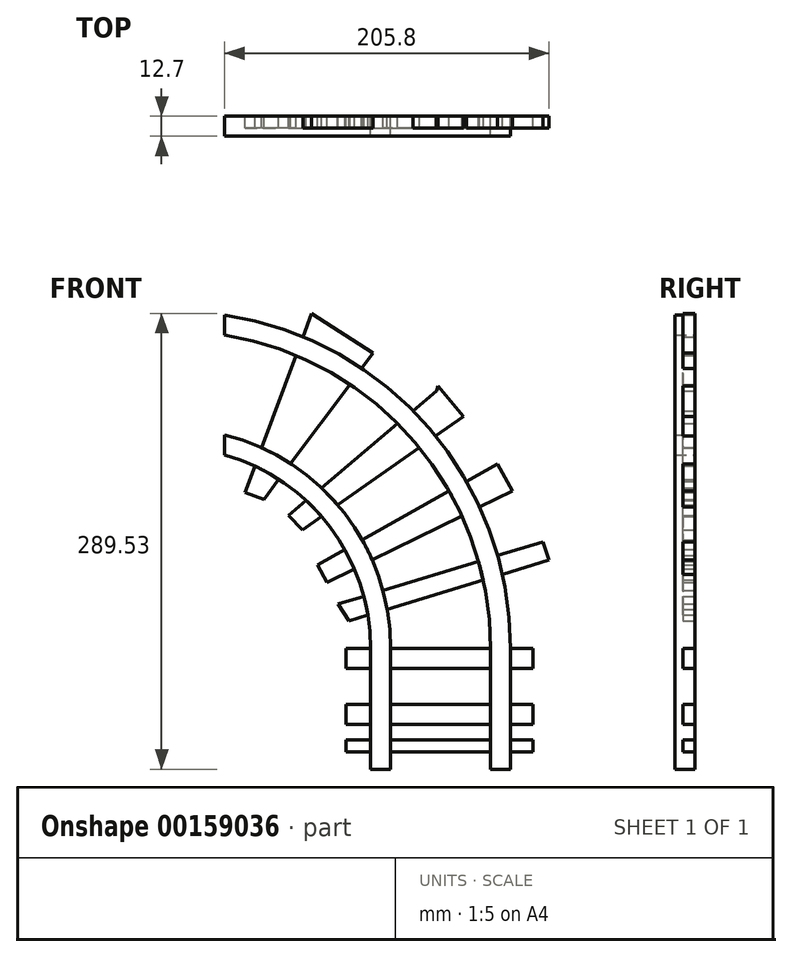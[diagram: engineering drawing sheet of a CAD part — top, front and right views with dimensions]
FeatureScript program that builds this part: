
annotation { "Feature Type Name" : "Feature", "Feature Type Description" : "" }
export const myFeature = defineFeature(function(context is Context, id is Id, definition is map)
    precondition{}
    {
        {
            var Q0;
            Q0=qCreatedBy(makeId("Front.planeOp"),FACE);
            var sketch = newSketch(context, id + "F0", { "sketchPlane" : qUnion([Q0])});
            skLineSegment(sketch, "E0", {"start": v(-50.34, 0) * mm, "end": v(-37.64, 0) * mm});
            skLineSegment(sketch, "E1", {"start": v(-37.64, 0) * mm, "end": v(-37.64, -76.88) * mm});
            skLineSegment(sketch, "E2", {"start": v(-50.34, 0) * mm, "end": v(-50.34, -76.88) * mm});
            skLineSegment(sketch, "E3", {"start": v(-50.34, -76.88) * mm, "end": v(-37.64, -76.88) * mm});
            skLineSegment(sketch, "E4", {"start": v(25.86, 0) * mm, "end": v(25.86, -76.88) * mm});
            skLineSegment(sketch, "E5", {"start": v(25.86, -76.88) * mm, "end": v(38.56, -76.88) * mm});
            skLineSegment(sketch, "E6", {"start": v(38.56, -76.88) * mm, "end": v(38.56, 0) * mm});
            skLineSegment(sketch, "E7", {"start": v(38.56, 0) * mm, "end": v(25.86, 0) * mm});
            skArc(sketch, "E8", {"start": v(-50.34, 0) * mm, "mid": v(-76.12, 76.94) * mm, "end": v(-143.03, 122.84) * mm});
            skArc(sketch, "E9", {"start": v(-37.64, 0) * mm, "mid": v(-67.1, 85.84) * mm, "end": v(-143.03, 135.54) * mm});
            skArc(sketch, "E10", {"start": v(25.86, 0) * mm, "mid": v(-22.06, 130.52) * mm, "end": v(-143.03, 199.04) * mm});
            skArc(sketch, "E11", {"start": v(38.56, 0) * mm, "mid": v(-13.06, 139.47) * mm, "end": v(-143.03, 211.74) * mm});
            skLineSegment(sketch, "E12", {"start": v(-143.03, 211.74) * mm, "end": v(-143.03, 199.04) * mm});
            skLineSegment(sketch, "E13", {"start": v(-143.03, 135.54) * mm, "end": v(-143.03, 122.84) * mm});
            skLineSegment(sketch, "E14", {"start": v(-65.9, -35.56) * mm, "end": v(-65.9, -48.26) * mm});
            skLineSegment(sketch, "E15", {"start": v(-65.9, -48.26) * mm, "end": v(52.66, -48.26) * mm});
            skLineSegment(sketch, "E16", {"start": v(52.66, -48.26) * mm, "end": v(52.66, -35.56) * mm});
            skLineSegment(sketch, "E17", {"start": v(52.66, -35.56) * mm, "end": v(-65.9, -35.56) * mm});
            skLineSegment(sketch, "E18", {"start": v(-65.9, 0) * mm, "end": v(-65.9, -12.7) * mm});
            skLineSegment(sketch, "E19", {"start": v(-65.9, -12.7) * mm, "end": v(52.66, -12.7) * mm});
            skLineSegment(sketch, "E20", {"start": v(52.66, -12.7) * mm, "end": v(52.66, 0) * mm});
            skLineSegment(sketch, "E21", {"start": v(52.66, 0) * mm, "end": v(-65.9, 0) * mm});
            skLineSegment(sketch, "E22", {"start": v(-48.75, 187.4) * mm, "end": v(-87.85, 212.65) * mm});
            skLineSegment(sketch, "E23", {"start": v(-87.85, 212.65) * mm, "end": v(-130.11, 98.99) * mm});
            skLineSegment(sketch, "E24", {"start": v(-130.11, 98.99) * mm, "end": v(-118.21, 94.56) * mm});
            skLineSegment(sketch, "E25", {"start": v(-118.21, 94.56) * mm, "end": v(-48.75, 187.4) * mm});
            skLineSegment(sketch, "E26", {"start": v(-78.05, 41.82) * mm, "end": v(-84.25, 52.9) * mm});
            skLineSegment(sketch, "E27", {"start": v(-84.25, 52.9) * mm, "end": v(30.17, 116.9) * mm});
            skLineSegment(sketch, "E28", {"start": v(39.65, 99.94) * mm, "end": v(-78.05, 41.82) * mm});
            skLineSegment(sketch, "E29", {"start": v(30.17, 116.9) * mm, "end": v(39.65, 99.94) * mm});
            skLineSegment(sketch, "E30", {"start": v(39.65, 99.94) * mm, "end": v(39.65, 99.94) * mm});
            skLineSegment(sketch, "E31", {"start": v(-70.95, 28) * mm, "end": v(59.22, 67.6) * mm});
            skLineSegment(sketch, "E32", {"start": v(59.22, 67.6) * mm, "end": v(62.77, 55.95) * mm});
            skLineSegment(sketch, "E33", {"start": v(62.77, 55.95) * mm, "end": v(-63.98, 17.37) * mm});
            skLineSegment(sketch, "E34", {"start": v(-70.95, 28) * mm, "end": v(-63.98, 17.37) * mm});
            skLineSegment(sketch, "E35", {"start": v(-102.62, 84.2) * mm, "end": v(-93.77, 75.1) * mm});
            skLineSegment(sketch, "E36", {"start": v(-102.62, 84.2) * mm, "end": v(-8.48, 163.47) * mm});
            skLineSegment(sketch, "E37", {"start": v(-93.77, 75.1) * mm, "end": v(8.75, 147.3) * mm});
            skLineSegment(sketch, "E38", {"start": v(8.75, 147.3) * mm, "end": v(-7.49, 166.59) * mm});
            skLineSegment(sketch, "E39", {"start": v(-7.49, 166.59) * mm, "end": v(-8.48, 163.47) * mm});
            skLineSegment(sketch, "E40", {"start": v(-65.9, -58.2) * mm, "end": v(-65.9, -65.83) * mm});
            skLineSegment(sketch, "E41", {"start": v(-65.9, -65.83) * mm, "end": v(52.66, -65.83) * mm});
            skLineSegment(sketch, "E42", {"start": v(52.66, -65.83) * mm, "end": v(52.66, -58.2) * mm});
            skLineSegment(sketch, "E43", {"start": v(52.66, -58.2) * mm, "end": v(-65.9, -58.2) * mm});
            skSolve(sketch);
        }
        {
            var Q0;
            {var subQ0=sQuery(id+"F0.wireOp",EDGE,"E13");Q0=makeQuery(id+"F0.imprint","IMPRINT",FACE,{"disambiguationData":[TD([[makeQuery(id+"F0.imprint","IMPRINT",EDGE,{"derivedFrom":subQ0}),1.0]])]});}
            var Q1;
            {var subQ0=sQuery(id+"F0.wireOp",EDGE,"E25");var subQ1=sQuery(id+"F0.wireOp",EDGE,"E8");var subQ2=makeQuery(id+"F0.imprint","INTERSECT",VERTEX,{"derivedFrom":[subQ1,subQ0]});Q1=makeQuery(id+"F0.imprint","IMPRINT",FACE,{"disambiguationData":[TD([[makeQuery(id+"F0.imprint","IMPRINT",EDGE,{"disambiguationData":[TD([[subQ2,-1.0]])],"derivedFrom":subQ1}),-1.0]])]});}
            var Q2;
            {var subQ0=sQuery(id+"F0.wireOp",EDGE,"E36");var subQ1=sQuery(id+"F0.wireOp",EDGE,"E8");var subQ2=makeQuery(id+"F0.imprint","INTERSECT",VERTEX,{"derivedFrom":[subQ1,subQ0]});Q2=makeQuery(id+"F0.imprint","IMPRINT",FACE,{"disambiguationData":[TD([[makeQuery(id+"F0.imprint","IMPRINT",EDGE,{"disambiguationData":[TD([[subQ2,-1.0]])],"derivedFrom":subQ1}),-1.0]])]});}
            var Q3;
            {var subQ0=sQuery(id+"F0.wireOp",EDGE,"E37");var subQ1=sQuery(id+"F0.wireOp",EDGE,"E8");var subQ2=makeQuery(id+"F0.imprint","INTERSECT",VERTEX,{"derivedFrom":[subQ1,subQ0]});Q3=makeQuery(id+"F0.imprint","IMPRINT",FACE,{"disambiguationData":[TD([[makeQuery(id+"F0.imprint","IMPRINT",EDGE,{"disambiguationData":[TD([[subQ2,-1.0]])],"derivedFrom":subQ1}),-1.0]])]});}
            var Q4;
            {var subQ0=sQuery(id+"F0.wireOp",EDGE,"E27");var subQ1=sQuery(id+"F0.wireOp",EDGE,"E8");var subQ2=makeQuery(id+"F0.imprint","INTERSECT",VERTEX,{"derivedFrom":[subQ1,subQ0]});Q4=makeQuery(id+"F0.imprint","IMPRINT",FACE,{"disambiguationData":[TD([[makeQuery(id+"F0.imprint","IMPRINT",EDGE,{"disambiguationData":[TD([[subQ2,-1.0]])],"derivedFrom":subQ1}),-1.0]])]});}
            var Q5;
            {var subQ0=sQuery(id+"F0.wireOp",EDGE,"E28");var subQ1=sQuery(id+"F0.wireOp",EDGE,"E8");var subQ2=makeQuery(id+"F0.imprint","INTERSECT",VERTEX,{"derivedFrom":[subQ1,subQ0]});Q5=makeQuery(id+"F0.imprint","IMPRINT",FACE,{"disambiguationData":[TD([[makeQuery(id+"F0.imprint","IMPRINT",EDGE,{"disambiguationData":[TD([[subQ2,-1.0]])],"derivedFrom":subQ1}),-1.0]])]});}
            var Q6;
            {var subQ0=sQuery(id+"F0.wireOp",EDGE,"E31");var subQ1=sQuery(id+"F0.wireOp",EDGE,"E8");var subQ2=makeQuery(id+"F0.imprint","INTERSECT",VERTEX,{"derivedFrom":[subQ1,subQ0]});Q6=makeQuery(id+"F0.imprint","IMPRINT",FACE,{"disambiguationData":[TD([[makeQuery(id+"F0.imprint","IMPRINT",EDGE,{"disambiguationData":[TD([[subQ2,-1.0]])],"derivedFrom":subQ1}),-1.0]])]});}
            var Q7;
            {var subQ0=sQuery(id+"F0.wireOp",EDGE,"E33");var subQ1=sQuery(id+"F0.wireOp",EDGE,"E8");var subQ2=makeQuery(id+"F0.imprint","INTERSECT",VERTEX,{"derivedFrom":[subQ1,subQ0]});Q7=makeQuery(id+"F0.imprint","IMPRINT",FACE,{"disambiguationData":[TD([[makeQuery(id+"F0.imprint","IMPRINT",EDGE,{"disambiguationData":[TD([[subQ2,-1.0]])],"derivedFrom":subQ1}),-1.0]])]});}
            var Q8;
            {var subQ1=sQuery(id+"F0.wireOp",EDGE,"E8");var subQ3=sQuery(id+"F0.wireOp",EDGE,"E33");var subQ4=makeQuery(id+"F0.imprint","INTERSECT",VERTEX,{"derivedFrom":[subQ1,subQ3]});Q8=makeQuery(id+"F0.imprint","IMPRINT",FACE,{"disambiguationData":[TD([[makeQuery(id+"F0.imprint","IMPRINT",EDGE,{"disambiguationData":[TD([[subQ4,1.0]])],"derivedFrom":subQ3}),1.0]])]});}
            var Q9;
            {var subQ3=sQuery(id+"F0.wireOp",EDGE,"E19");var subQ5=sQuery(id+"F0.wireOp",EDGE,"E2");var subQ7=makeQuery(id+"F0.imprint","INTERSECT",VERTEX,{"derivedFrom":[subQ5,subQ3]});Q9=makeQuery(id+"F0.imprint","IMPRINT",FACE,{"disambiguationData":[TD([[makeQuery(id+"F0.imprint","IMPRINT",EDGE,{"disambiguationData":[TD([[subQ7,-1.0]])],"derivedFrom":subQ3}),1.0]])]});}
            var Q10;
            {var subQ0=sQuery(id+"F0.wireOp",EDGE,"E19");var subQ1=sQuery(id+"F0.wireOp",EDGE,"E1");var subQ2=makeQuery(id+"F0.imprint","INTERSECT",VERTEX,{"derivedFrom":[subQ1,subQ0]});Q10=makeQuery(id+"F0.imprint","IMPRINT",FACE,{"disambiguationData":[TD([[makeQuery(id+"F0.imprint","IMPRINT",EDGE,{"disambiguationData":[TD([[subQ2,-1.0]])],"derivedFrom":subQ1}),-1.0]])]});}
            var Q11;
            {var subQ0=sQuery(id+"F0.wireOp",EDGE,"E17");var subQ1=sQuery(id+"F0.wireOp",EDGE,"E1");var subQ2=makeQuery(id+"F0.imprint","INTERSECT",VERTEX,{"derivedFrom":[subQ1,subQ0]});Q11=makeQuery(id+"F0.imprint","IMPRINT",FACE,{"disambiguationData":[TD([[makeQuery(id+"F0.imprint","IMPRINT",EDGE,{"disambiguationData":[TD([[subQ2,-1.0]])],"derivedFrom":subQ1}),-1.0]])]});}
            var Q12;
            {var subQ0=sQuery(id+"F0.wireOp",EDGE,"E15");var subQ1=sQuery(id+"F0.wireOp",EDGE,"E1");var subQ2=makeQuery(id+"F0.imprint","INTERSECT",VERTEX,{"derivedFrom":[subQ1,subQ0]});Q12=makeQuery(id+"F0.imprint","IMPRINT",FACE,{"disambiguationData":[TD([[makeQuery(id+"F0.imprint","IMPRINT",EDGE,{"disambiguationData":[TD([[subQ2,-1.0]])],"derivedFrom":subQ1}),-1.0]])]});}
            var Q13;
            {var subQ0=sQuery(id+"F0.wireOp",EDGE,"E41");var subQ1=sQuery(id+"F0.wireOp",EDGE,"E1");var subQ2=makeQuery(id+"F0.imprint","INTERSECT",VERTEX,{"derivedFrom":[subQ1,subQ0]});Q13=makeQuery(id+"F0.imprint","IMPRINT",FACE,{"disambiguationData":[TD([[makeQuery(id+"F0.imprint","IMPRINT",EDGE,{"disambiguationData":[TD([[subQ2,1.0]])],"derivedFrom":subQ1}),-1.0]])]});}
            var Q14;
            {var subQ0=sQuery(id+"F0.wireOp",EDGE,"E3");Q14=makeQuery(id+"F0.imprint","IMPRINT",FACE,{"disambiguationData":[TD([[makeQuery(id+"F0.imprint","IMPRINT",EDGE,{"derivedFrom":subQ0}),1.0]])]});}
            var Q15;
            {var subQ0=sQuery(id+"F0.wireOp",EDGE,"E5");Q15=makeQuery(id+"F0.imprint","IMPRINT",FACE,{"disambiguationData":[TD([[makeQuery(id+"F0.imprint","IMPRINT",EDGE,{"derivedFrom":subQ0}),1.0]])]});}
            var Q16;
            {var subQ0=sQuery(id+"F0.wireOp",EDGE,"E41");var subQ1=sQuery(id+"F0.wireOp",EDGE,"E4");var subQ2=makeQuery(id+"F0.imprint","INTERSECT",VERTEX,{"derivedFrom":[subQ1,subQ0]});Q16=makeQuery(id+"F0.imprint","IMPRINT",FACE,{"disambiguationData":[TD([[makeQuery(id+"F0.imprint","IMPRINT",EDGE,{"disambiguationData":[TD([[subQ2,1.0]])],"derivedFrom":subQ1}),1.0]])]});}
            var Q17;
            {var subQ0=sQuery(id+"F0.wireOp",EDGE,"E15");var subQ1=sQuery(id+"F0.wireOp",EDGE,"E4");var subQ2=makeQuery(id+"F0.imprint","INTERSECT",VERTEX,{"derivedFrom":[subQ1,subQ0]});Q17=makeQuery(id+"F0.imprint","IMPRINT",FACE,{"disambiguationData":[TD([[makeQuery(id+"F0.imprint","IMPRINT",EDGE,{"disambiguationData":[TD([[subQ2,-1.0]])],"derivedFrom":subQ1}),1.0]])]});}
            var Q18;
            {var subQ0=sQuery(id+"F0.wireOp",EDGE,"E17");var subQ1=sQuery(id+"F0.wireOp",EDGE,"E4");var subQ2=makeQuery(id+"F0.imprint","INTERSECT",VERTEX,{"derivedFrom":[subQ1,subQ0]});Q18=makeQuery(id+"F0.imprint","IMPRINT",FACE,{"disambiguationData":[TD([[makeQuery(id+"F0.imprint","IMPRINT",EDGE,{"disambiguationData":[TD([[subQ2,-1.0]])],"derivedFrom":subQ1}),1.0]])]});}
            var Q19;
            {var subQ0=sQuery(id+"F0.wireOp",EDGE,"E19");var subQ1=sQuery(id+"F0.wireOp",EDGE,"E4");var subQ2=makeQuery(id+"F0.imprint","INTERSECT",VERTEX,{"derivedFrom":[subQ1,subQ0]});Q19=makeQuery(id+"F0.imprint","IMPRINT",FACE,{"disambiguationData":[TD([[makeQuery(id+"F0.imprint","IMPRINT",EDGE,{"disambiguationData":[TD([[subQ2,-1.0]])],"derivedFrom":subQ1}),1.0]])]});}
            var Q20;
            {var subQ3=sQuery(id+"F0.wireOp",EDGE,"E19");var subQ5=sQuery(id+"F0.wireOp",EDGE,"E6");var subQ7=makeQuery(id+"F0.imprint","INTERSECT",VERTEX,{"derivedFrom":[subQ5,subQ3]});Q20=makeQuery(id+"F0.imprint","IMPRINT",FACE,{"disambiguationData":[TD([[makeQuery(id+"F0.imprint","IMPRINT",EDGE,{"disambiguationData":[TD([[subQ7,1.0]])],"derivedFrom":subQ3}),1.0]])]});}
            var Q21;
            {var subQ3=sQuery(id+"F0.wireOp",EDGE,"E33");var subQ5=sQuery(id+"F0.wireOp",EDGE,"E11");var subQ6=makeQuery(id+"F0.imprint","INTERSECT",VERTEX,{"derivedFrom":[subQ5,subQ3]});Q21=makeQuery(id+"F0.imprint","IMPRINT",FACE,{"disambiguationData":[TD([[makeQuery(id+"F0.imprint","IMPRINT",EDGE,{"disambiguationData":[TD([[subQ6,-1.0]])],"derivedFrom":subQ3}),1.0]])]});}
            var Q22;
            {var subQ0=sQuery(id+"F0.wireOp",EDGE,"E33");var subQ1=sQuery(id+"F0.wireOp",EDGE,"E10");var subQ2=makeQuery(id+"F0.imprint","INTERSECT",VERTEX,{"derivedFrom":[subQ1,subQ0]});Q22=makeQuery(id+"F0.imprint","IMPRINT",FACE,{"disambiguationData":[TD([[makeQuery(id+"F0.imprint","IMPRINT",EDGE,{"disambiguationData":[TD([[subQ2,-1.0]])],"derivedFrom":subQ1}),-1.0]])]});}
            var Q23;
            {var subQ0=sQuery(id+"F0.wireOp",EDGE,"E31");var subQ1=sQuery(id+"F0.wireOp",EDGE,"E10");var subQ2=makeQuery(id+"F0.imprint","INTERSECT",VERTEX,{"derivedFrom":[subQ1,subQ0]});Q23=makeQuery(id+"F0.imprint","IMPRINT",FACE,{"disambiguationData":[TD([[makeQuery(id+"F0.imprint","IMPRINT",EDGE,{"disambiguationData":[TD([[subQ2,-1.0]])],"derivedFrom":subQ1}),-1.0]])]});}
            var Q24;
            {var subQ0=sQuery(id+"F0.wireOp",EDGE,"E28");var subQ1=sQuery(id+"F0.wireOp",EDGE,"E10");var subQ2=makeQuery(id+"F0.imprint","INTERSECT",VERTEX,{"derivedFrom":[subQ1,subQ0]});Q24=makeQuery(id+"F0.imprint","IMPRINT",FACE,{"disambiguationData":[TD([[makeQuery(id+"F0.imprint","IMPRINT",EDGE,{"disambiguationData":[TD([[subQ2,-1.0]])],"derivedFrom":subQ1}),-1.0]])]});}
            var Q25;
            {var subQ0=sQuery(id+"F0.wireOp",EDGE,"E27");var subQ1=sQuery(id+"F0.wireOp",EDGE,"E10");var subQ2=makeQuery(id+"F0.imprint","INTERSECT",VERTEX,{"derivedFrom":[subQ1,subQ0]});Q25=makeQuery(id+"F0.imprint","IMPRINT",FACE,{"disambiguationData":[TD([[makeQuery(id+"F0.imprint","IMPRINT",EDGE,{"disambiguationData":[TD([[subQ2,-1.0]])],"derivedFrom":subQ1}),-1.0]])]});}
            var Q26;
            {var subQ0=sQuery(id+"F0.wireOp",EDGE,"E37");var subQ1=sQuery(id+"F0.wireOp",EDGE,"E10");var subQ2=makeQuery(id+"F0.imprint","INTERSECT",VERTEX,{"derivedFrom":[subQ1,subQ0]});Q26=makeQuery(id+"F0.imprint","IMPRINT",FACE,{"disambiguationData":[TD([[makeQuery(id+"F0.imprint","IMPRINT",EDGE,{"disambiguationData":[TD([[subQ2,-1.0]])],"derivedFrom":subQ1}),-1.0]])]});}
            var Q27;
            {var subQ0=sQuery(id+"F0.wireOp",EDGE,"E36");var subQ1=sQuery(id+"F0.wireOp",EDGE,"E10");var subQ2=makeQuery(id+"F0.imprint","INTERSECT",VERTEX,{"derivedFrom":[subQ1,subQ0]});Q27=makeQuery(id+"F0.imprint","IMPRINT",FACE,{"disambiguationData":[TD([[makeQuery(id+"F0.imprint","IMPRINT",EDGE,{"disambiguationData":[TD([[subQ2,-1.0]])],"derivedFrom":subQ1}),-1.0]])]});}
            var Q28;
            {var subQ0=sQuery(id+"F0.wireOp",EDGE,"E23");var subQ1=sQuery(id+"F0.wireOp",EDGE,"E10");var subQ2=makeQuery(id+"F0.imprint","INTERSECT",VERTEX,{"derivedFrom":[subQ1,subQ0]});Q28=makeQuery(id+"F0.imprint","IMPRINT",FACE,{"disambiguationData":[TD([[makeQuery(id+"F0.imprint","IMPRINT",EDGE,{"disambiguationData":[TD([[subQ2,1.0]])],"derivedFrom":subQ1}),-1.0]])]});}
            var Q29;
            {var subQ0=sQuery(id+"F0.wireOp",EDGE,"E12");Q29=makeQuery(id+"F0.imprint","IMPRINT",FACE,{"disambiguationData":[TD([[makeQuery(id+"F0.imprint","IMPRINT",EDGE,{"derivedFrom":subQ0}),1.0]])]});}
            extrude(context, id + "F1", {"entities" : qUnion([Q0, Q1, Q2, Q3, Q4, Q5, Q6, Q7, Q8, Q9, Q10, Q11, Q12, Q13, Q14, Q15, Q16, Q17, Q18, Q19, Q20, Q21, Q22, Q23, Q24, Q25, Q26, Q27, Q28, Q29]), "depth" : 12.7 * mm});
        }
        {
            var Q0;
            {var subQ5=sQuery(id+"F0.wireOp",EDGE,"E24");Q0=makeQuery(id+"F0.imprint","IMPRINT",FACE,{"disambiguationData":[TD([[makeQuery(id+"F0.imprint","IMPRINT",EDGE,{"derivedFrom":subQ5}),1.0]])]});}
            var Q1;
            {var subQ0=sQuery(id+"F0.wireOp",EDGE,"E23");var subQ1=sQuery(id+"F0.wireOp",EDGE,"E9");var subQ2=makeQuery(id+"F0.imprint","INTERSECT",VERTEX,{"derivedFrom":[subQ1,subQ0]});Q1=makeQuery(id+"F0.imprint","IMPRINT",FACE,{"disambiguationData":[TD([[makeQuery(id+"F0.imprint","IMPRINT",EDGE,{"disambiguationData":[TD([[subQ2,1.0]])],"derivedFrom":subQ1}),-1.0]])]});}
            var Q2;
            {var subQ5=sQuery(id+"F0.wireOp",EDGE,"E22");Q2=makeQuery(id+"F0.imprint","IMPRINT",FACE,{"disambiguationData":[TD([[makeQuery(id+"F0.imprint","IMPRINT",EDGE,{"derivedFrom":subQ5}),1.0]])]});}
            var Q3;
            {var subQ0=sQuery(id+"F0.wireOp",EDGE,"E38");Q3=makeQuery(id+"F0.imprint","IMPRINT",FACE,{"disambiguationData":[TD([[makeQuery(id+"F0.imprint","IMPRINT",EDGE,{"derivedFrom":subQ0}),1.0]])]});}
            var Q4;
            {var subQ0=sQuery(id+"F0.wireOp",EDGE,"E37");var subQ1=sQuery(id+"F0.wireOp",EDGE,"E9");var subQ2=makeQuery(id+"F0.imprint","INTERSECT",VERTEX,{"derivedFrom":[subQ1,subQ0]});Q4=makeQuery(id+"F0.imprint","IMPRINT",FACE,{"disambiguationData":[TD([[makeQuery(id+"F0.imprint","IMPRINT",EDGE,{"disambiguationData":[TD([[subQ2,-1.0]])],"derivedFrom":subQ1}),-1.0]])]});}
            var Q5;
            {var subQ5=sQuery(id+"F0.wireOp",EDGE,"E35");Q5=makeQuery(id+"F0.imprint","IMPRINT",FACE,{"disambiguationData":[TD([[makeQuery(id+"F0.imprint","IMPRINT",EDGE,{"derivedFrom":subQ5}),1.0]])]});}
            var Q6;
            {var subQ5=sQuery(id+"F0.wireOp",EDGE,"E26");Q6=makeQuery(id+"F0.imprint","IMPRINT",FACE,{"disambiguationData":[TD([[makeQuery(id+"F0.imprint","IMPRINT",EDGE,{"derivedFrom":subQ5}),-1.0]])]});}
            var Q7;
            {var subQ0=sQuery(id+"F0.wireOp",EDGE,"E28");var subQ1=sQuery(id+"F0.wireOp",EDGE,"E9");var subQ2=makeQuery(id+"F0.imprint","INTERSECT",VERTEX,{"derivedFrom":[subQ1,subQ0]});Q7=makeQuery(id+"F0.imprint","IMPRINT",FACE,{"disambiguationData":[TD([[makeQuery(id+"F0.imprint","IMPRINT",EDGE,{"disambiguationData":[TD([[subQ2,-1.0]])],"derivedFrom":subQ1}),-1.0]])]});}
            var Q8;
            {var subQ4=sQuery(id+"F0.wireOp",EDGE,"E29");Q8=makeQuery(id+"F0.imprint","IMPRINT",FACE,{"disambiguationData":[TD([[makeQuery(id+"F0.imprint","IMPRINT",EDGE,{"derivedFrom":subQ4}),-1.0]])]});}
            var Q9;
            {var subQ5=sQuery(id+"F0.wireOp",EDGE,"E32");Q9=makeQuery(id+"F0.imprint","IMPRINT",FACE,{"disambiguationData":[TD([[makeQuery(id+"F0.imprint","IMPRINT",EDGE,{"derivedFrom":subQ5}),-1.0]])]});}
            var Q10;
            {var subQ0=sQuery(id+"F0.wireOp",EDGE,"E33");var subQ1=sQuery(id+"F0.wireOp",EDGE,"E9");var subQ2=makeQuery(id+"F0.imprint","INTERSECT",VERTEX,{"derivedFrom":[subQ1,subQ0]});Q10=makeQuery(id+"F0.imprint","IMPRINT",FACE,{"disambiguationData":[TD([[makeQuery(id+"F0.imprint","IMPRINT",EDGE,{"disambiguationData":[TD([[subQ2,-1.0]])],"derivedFrom":subQ1}),-1.0]])]});}
            var Q11;
            {var subQ5=sQuery(id+"F0.wireOp",EDGE,"E34");Q11=makeQuery(id+"F0.imprint","IMPRINT",FACE,{"disambiguationData":[TD([[makeQuery(id+"F0.imprint","IMPRINT",EDGE,{"derivedFrom":subQ5}),1.0]])]});}
            var Q12;
            {var subQ5=sQuery(id+"F0.wireOp",EDGE,"E18");Q12=makeQuery(id+"F0.imprint","IMPRINT",FACE,{"disambiguationData":[TD([[makeQuery(id+"F0.imprint","IMPRINT",EDGE,{"derivedFrom":subQ5}),1.0]])]});}
            var Q13;
            {var subQ5=sQuery(id+"F0.wireOp",EDGE,"E14");Q13=makeQuery(id+"F0.imprint","IMPRINT",FACE,{"disambiguationData":[TD([[makeQuery(id+"F0.imprint","IMPRINT",EDGE,{"derivedFrom":subQ5}),1.0]])]});}
            var Q14;
            {var subQ5=sQuery(id+"F0.wireOp",EDGE,"E40");Q14=makeQuery(id+"F0.imprint","IMPRINT",FACE,{"disambiguationData":[TD([[makeQuery(id+"F0.imprint","IMPRINT",EDGE,{"derivedFrom":subQ5}),1.0]])]});}
            var Q15;
            {var subQ0=sQuery(id+"F0.wireOp",EDGE,"E41");var subQ1=sQuery(id+"F0.wireOp",EDGE,"E1");var subQ2=makeQuery(id+"F0.imprint","INTERSECT",VERTEX,{"derivedFrom":[subQ1,subQ0]});Q15=makeQuery(id+"F0.imprint","IMPRINT",FACE,{"disambiguationData":[TD([[makeQuery(id+"F0.imprint","IMPRINT",EDGE,{"disambiguationData":[TD([[subQ2,1.0]])],"derivedFrom":subQ1}),1.0]])]});}
            var Q16;
            {var subQ0=sQuery(id+"F0.wireOp",EDGE,"E17");var subQ1=sQuery(id+"F0.wireOp",EDGE,"E1");var subQ2=makeQuery(id+"F0.imprint","INTERSECT",VERTEX,{"derivedFrom":[subQ1,subQ0]});Q16=makeQuery(id+"F0.imprint","IMPRINT",FACE,{"disambiguationData":[TD([[makeQuery(id+"F0.imprint","IMPRINT",EDGE,{"disambiguationData":[TD([[subQ2,-1.0]])],"derivedFrom":subQ1}),1.0]])]});}
            var Q17;
            {var subQ1=sQuery(id+"F0.wireOp",EDGE,"E1");var subQ3=sQuery(id+"F0.wireOp",EDGE,"E19");var subQ4=makeQuery(id+"F0.imprint","INTERSECT",VERTEX,{"derivedFrom":[subQ1,subQ3]});Q17=makeQuery(id+"F0.imprint","IMPRINT",FACE,{"disambiguationData":[TD([[makeQuery(id+"F0.imprint","IMPRINT",EDGE,{"disambiguationData":[TD([[subQ4,-1.0]])],"derivedFrom":subQ3}),1.0]])]});}
            var Q18;
            {var subQ5=sQuery(id+"F0.wireOp",EDGE,"E20");Q18=makeQuery(id+"F0.imprint","IMPRINT",FACE,{"disambiguationData":[TD([[makeQuery(id+"F0.imprint","IMPRINT",EDGE,{"derivedFrom":subQ5}),1.0]])]});}
            var Q19;
            {var subQ5=sQuery(id+"F0.wireOp",EDGE,"E16");Q19=makeQuery(id+"F0.imprint","IMPRINT",FACE,{"disambiguationData":[TD([[makeQuery(id+"F0.imprint","IMPRINT",EDGE,{"derivedFrom":subQ5}),1.0]])]});}
            var Q20;
            {var subQ5=sQuery(id+"F0.wireOp",EDGE,"E42");Q20=makeQuery(id+"F0.imprint","IMPRINT",FACE,{"disambiguationData":[TD([[makeQuery(id+"F0.imprint","IMPRINT",EDGE,{"derivedFrom":subQ5}),1.0]])]});}
            extrude(context, id + "F2", {"entities" : qUnion([Q0, Q1, Q2, Q3, Q4, Q5, Q6, Q7, Q8, Q9, Q10, Q11, Q12, Q13, Q14, Q15, Q16, Q17, Q18, Q19, Q20]), "depth" : 7.62 * mm});
        }
    });
